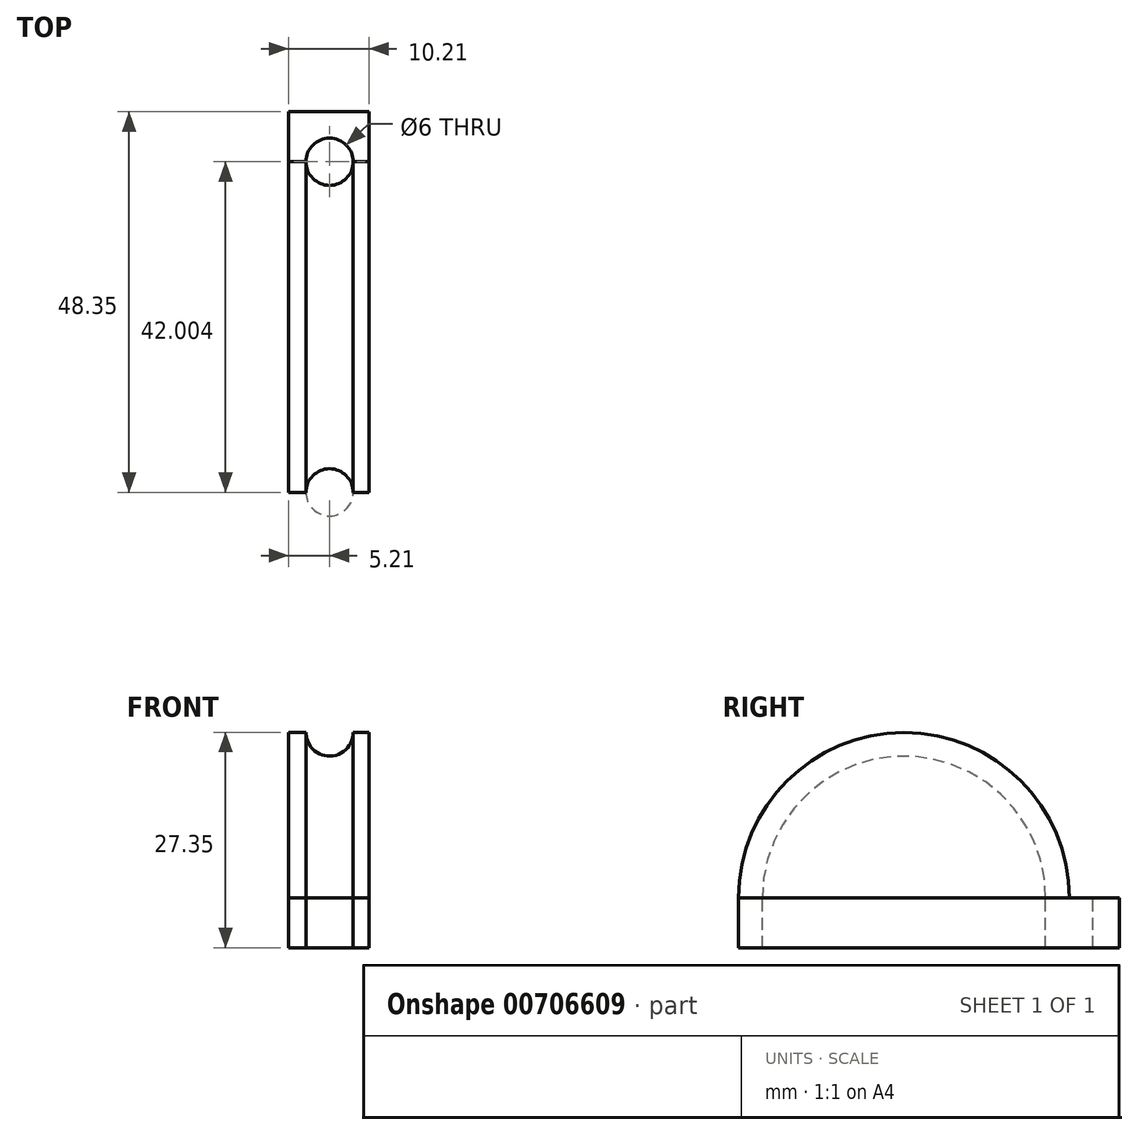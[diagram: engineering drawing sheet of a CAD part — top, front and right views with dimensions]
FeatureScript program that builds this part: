
annotation { "Feature Type Name" : "Feature", "Feature Type Description" : "" }
export const myFeature = defineFeature(function(context is Context, id is Id, definition is map)
    precondition{}
    {
        {
            var Q0;
            Q0=qCreatedBy(makeId("Top.planeOp"),FACE);
            var sketch = newSketch(context, id + "F0", { "sketchPlane" : qUnion([Q0])});
            skCircle(sketch, "E0", {"center": v(-11.43, 31.28) * mm, "radius": 3 * mm});
            skLineSegment(sketch, "E1.bottom", {"start": v(-16.64, 31.28) * mm, "end": v(-6.43, 31.28) * mm});
            skLineSegment(sketch, "E1.top", {"start": v(-16.64, 10.28) * mm, "end": v(-6.43, 10.28) * mm});
            skLineSegment(sketch, "E1.left", {"start": v(-16.64, 31.28) * mm, "end": v(-16.64, 10.28) * mm});
            skLineSegment(sketch, "E1.right", {"start": v(-6.43, 31.28) * mm, "end": v(-6.43, 10.28) * mm});
            skLineSegment(sketch, "E2.top", {"start": v(-16.64, 37.63) * mm, "end": v(-6.43, 37.63) * mm});
            skLineSegment(sketch, "E2.left", {"start": v(-16.64, 31.28) * mm, "end": v(-16.64, 37.63) * mm});
            skLineSegment(sketch, "E2.right", {"start": v(-6.43, 31.28) * mm, "end": v(-6.43, 37.63) * mm});
            skLineSegment(sketch, "E3.MirrorCS", {"start": v(-16.64, -10.72) * mm, "end": v(-16.64, 10.28) * mm});
            skCircle(sketch, "E4.MirrorC", {"center": v(-11.43, -10.72) * mm, "radius": 3 * mm});
            skLineSegment(sketch, "E5.MirrorCS", {"start": v(-6.43, -10.72) * mm, "end": v(-6.43, 10.28) * mm});
            skLineSegment(sketch, "E6.MirrorCS", {"start": v(-16.64, -10.72) * mm, "end": v(-6.43, -10.72) * mm});
            skSolve(sketch);
        }
        {
            var Q0;
            Q0=makeQuery(id+"F0.imprint","IMPRINT",FACE,{"disambiguationData":[TD([[makeQuery(id+"F0.imprint","IMPRINT",EDGE,{"derivedFrom":sQuery(id+"F0.wireOp",EDGE,"E1.top")}),1.0]])]});
            var Q1;
            Q1=sQuery(id+"F0.wireOp",EDGE,"E1.top");
            revolve(context, id + "F1", {"surfaceOperationType" : NewSurfaceOperationType.NEW, "entities" : qUnion([Q0]), "axis" : qUnion([Q1]), "revolveType" : RevolveType.ONE_DIRECTION, "angle" : 180 * degree});
        }
        {
            var Q0;
            Q0=makeQuery(id+"F0.imprint","IMPRINT",FACE,{"disambiguationData":[TD([[makeQuery(id+"F0.imprint","IMPRINT",EDGE,{"derivedFrom":sQuery(id+"F0.wireOp",EDGE,"E1.top")}),1.0]])]});
            var Q1;
            Q1=makeQuery(id+"F0.imprint","IMPRINT",FACE,{"disambiguationData":[TD([[makeQuery(id+"F0.imprint","IMPRINT",EDGE,{"derivedFrom":sQuery(id+"F0.wireOp",EDGE,"E1.top")}),-1.0]])]});
            var Q2;
            Q2=makeQuery(id+"F0.imprint","IMPRINT",FACE,{"disambiguationData":[TD([[makeQuery(id+"F0.imprint","IMPRINT",EDGE,{"derivedFrom":sQuery(id+"F0.wireOp",EDGE,"E2.top")}),-1.0]])]});
            extrude(context, id + "F2", {"entities" : qUnion([Q0, Q1, Q2]), "depth" : -6.35 * mm, "offsetDistance" : 25.4 * mm});
        }
    });
